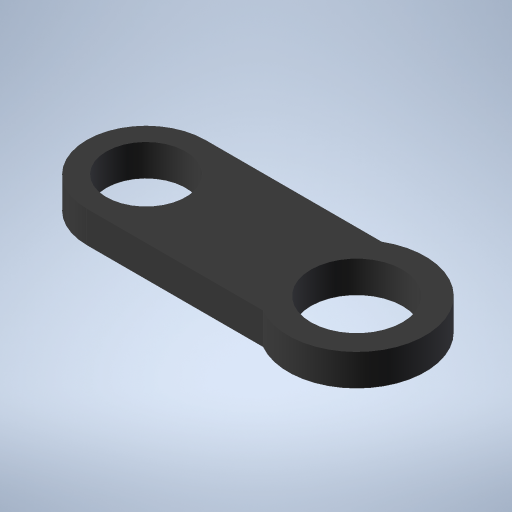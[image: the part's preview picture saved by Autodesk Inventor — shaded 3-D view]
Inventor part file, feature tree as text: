
AUTODESK INVENTOR PART (.ipt)
format: ipt  version: 2023 (Build 270158000, 158)  size: 235,520 bytes
history: native  units: in
note: dims shown in document units (in); Inventor stores cm internally (conversion verified against a paired STEP export)
features: extrude x1, sketch x1
ambient origin geometry x8: Origin, YZ Plane, XZ Plane, XY Plane, X Axis, Y Axis, Z Axis, Center Point
bodies: Solid1 (feature_tree)
feature tree (2):
  extrude  "Extrusion1"  Depth=1.125in
  sketch  "Sketch1"  dims[d5=0.3in d6=0.0in d11=0.755in d14=1.125in d15=0.871in d3=0.5in d4=0.0344in]
